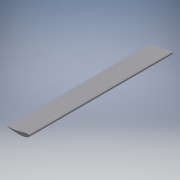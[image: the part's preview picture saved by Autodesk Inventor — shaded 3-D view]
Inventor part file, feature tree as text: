
AUTODESK INVENTOR PART (.ipt)
format: ipt  version: 2018.2 (Build 222227000, 227)  size: 143,360 bytes
history: native  units: mm
features: other x4, extrude x1, mirror x1, sketch x1, projected_geometry x1
ambient origin geometry x8: Origin, YZ Plane, XZ Plane, XY Plane, X Axis, Y Axis, Z Axis, Center Point
bodies: Body1 (feature_tree)
feature tree (8):
  other  "main frap.ipt"
  extrude  "押し出し2"  Depth=4.0mm
  mirror  "ミラー2"
  other  "ソリッド1::main frap.ipt"
  other  "TaggingFeature1"
  sketch  "スケッチ2"
  projected_geometry  "投影ループ2"
  other  "ソリッド1"
